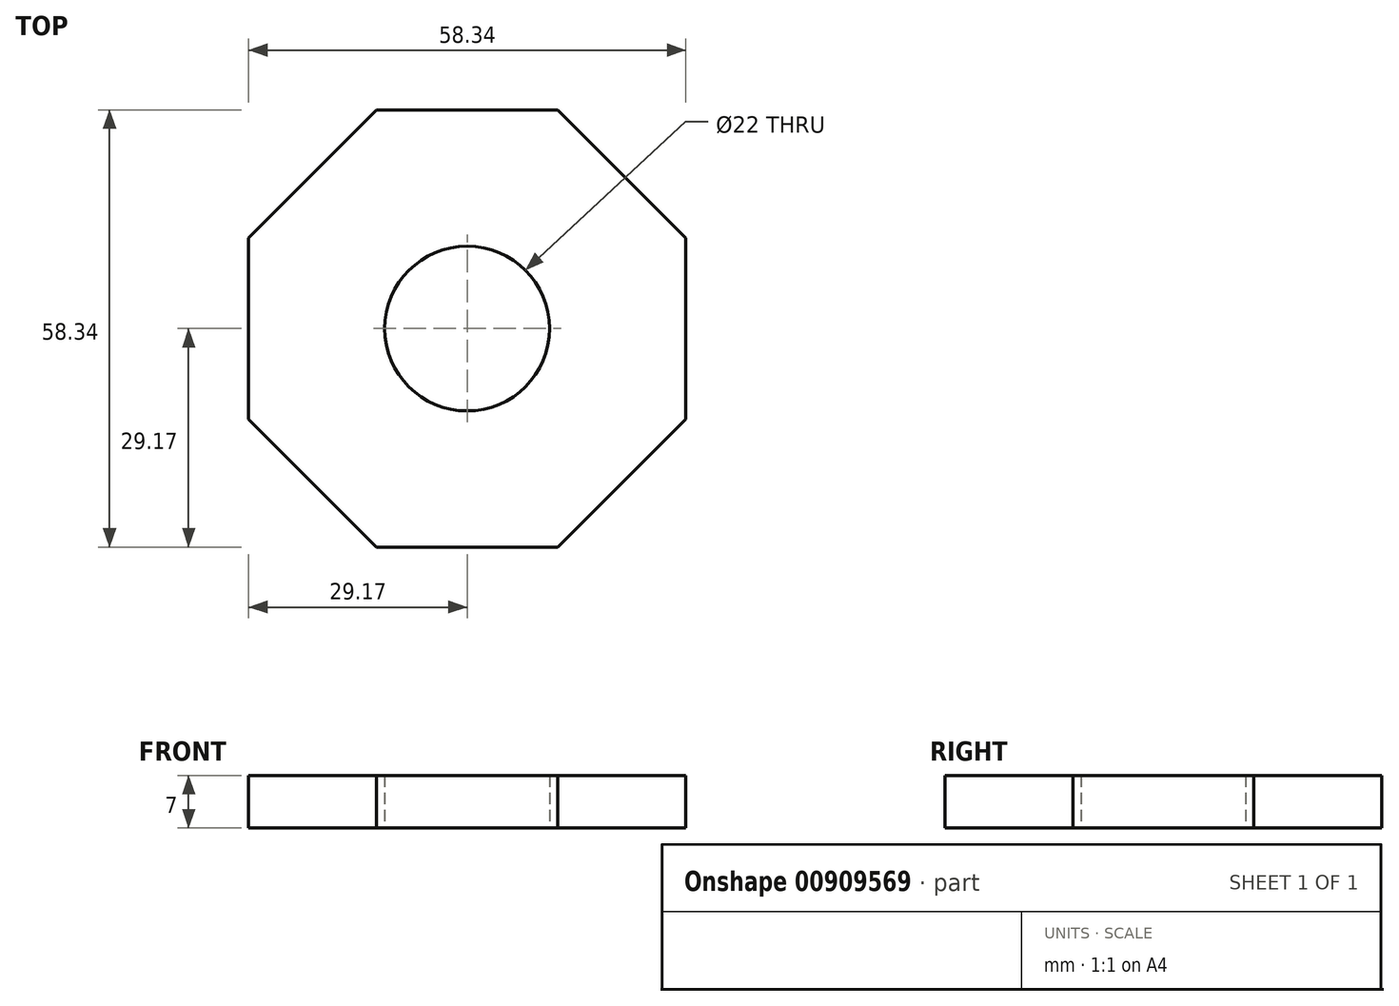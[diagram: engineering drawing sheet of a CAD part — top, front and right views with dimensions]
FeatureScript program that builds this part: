
annotation { "Feature Type Name" : "Feature", "Feature Type Description" : "" }
export const myFeature = defineFeature(function(context is Context, id is Id, definition is map)
    precondition{}
    {
        {
            var Q0;
            Q0=qCreatedBy(makeId("Top.planeOp"),FACE);
            var sketch = newSketch(context, id + "F0", { "sketchPlane" : qUnion([Q0])});
            skCircle(sketch, "E0", {"center": v(0, 0) * mm, "radius": 11 * mm});
            skCircle(sketch, "E1.cCircle", {"center": v(0, 0) * mm, "radius": 29.17 * mm, "construction": true});
            skLineSegment(sketch, "E1.0", {"start": v(-29.17, 12.08) * mm, "end": v(-12.08, 29.17) * mm});
            skLineSegment(sketch, "E1.1", {"start": v(-12.08, 29.17) * mm, "end": v(12.08, 29.17) * mm});
            skLineSegment(sketch, "E1.2", {"start": v(12.08, 29.17) * mm, "end": v(29.17, 12.08) * mm});
            skLineSegment(sketch, "E1.3", {"start": v(29.17, 12.08) * mm, "end": v(29.17, -12.08) * mm});
            skLineSegment(sketch, "E1.4", {"start": v(29.17, -12.08) * mm, "end": v(12.08, -29.17) * mm});
            skLineSegment(sketch, "E1.5", {"start": v(12.08, -29.17) * mm, "end": v(-12.08, -29.17) * mm});
            skLineSegment(sketch, "E1.6", {"start": v(-12.08, -29.17) * mm, "end": v(-29.17, -12.08) * mm});
            skLineSegment(sketch, "E1.7", {"start": v(-29.17, -12.08) * mm, "end": v(-29.17, 12.08) * mm});
            skPoint(sketch, "E1.0.midPoint", {"position": v(-20.62, 20.62) * mm});
            skSolve(sketch);
        }
        {
            var Q0;
            Q0=makeQuery(id+"F0.imprint","IMPRINT",FACE,{"disambiguationData":[TD([[makeQuery(id+"F0.imprint","IMPRINT",EDGE,{"derivedFrom":sQuery(id+"F0.wireOp",EDGE,"E0")}),-1.0]])]});
            extrude(context, id + "F1", {"entities" : qUnion([Q0]), "depth" : 7 * mm, "offsetDistance" : 25 * mm});
        }
    });
